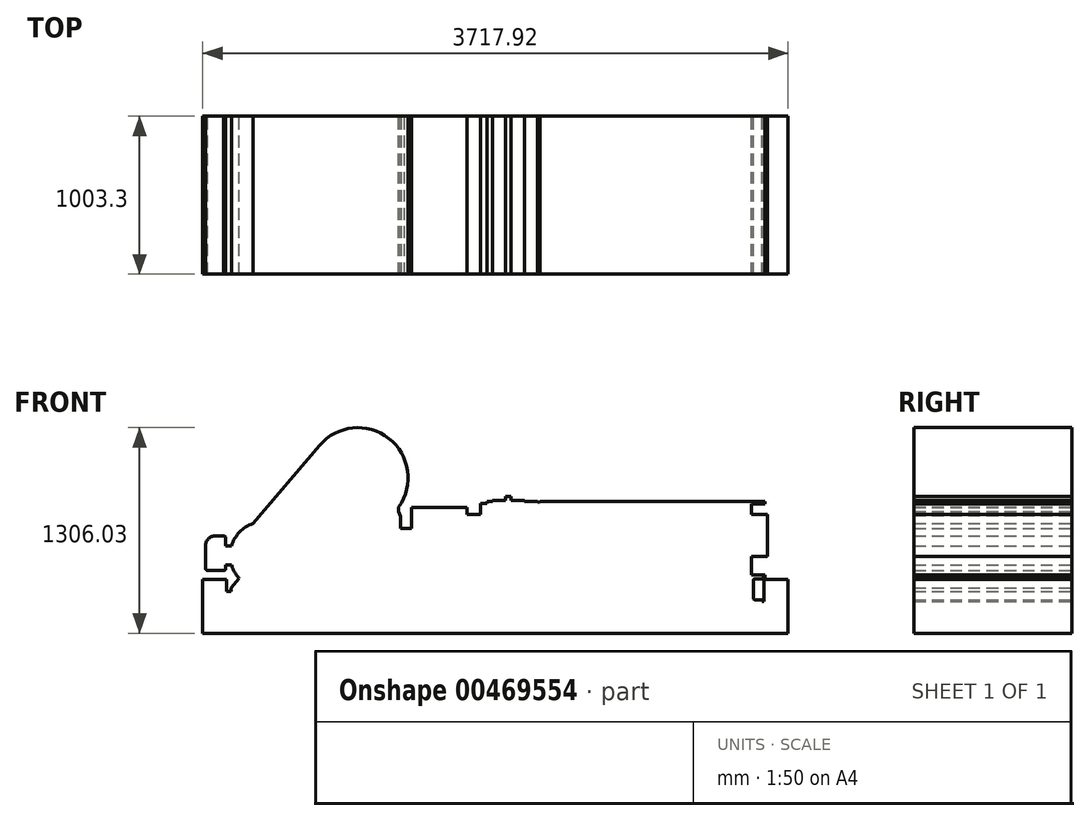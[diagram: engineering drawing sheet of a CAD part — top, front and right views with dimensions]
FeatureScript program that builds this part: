
annotation { "Feature Type Name" : "Feature", "Feature Type Description" : "" }
export const myFeature = defineFeature(function(context is Context, id is Id, definition is map)
    precondition{}
    {
        {
            var Q0;
            Q0=qCreatedBy(makeId("Front.planeOp"),FACE);
            var sketch = newSketch(context, id + "F0", { "sketchPlane" : qUnion([Q0])});
            skLineSegment(sketch, "E0", {"start": v(-2232.26, -692.1) * mm, "end": v(-2341.03, -692.1) * mm});
            skLineSegment(sketch, "E1", {"start": v(-2232.2, -756.28) * mm, "end": v(-2232.2, -692.78) * mm});
            skLineSegment(sketch, "E2", {"start": v(-2939.48, -959.48) * mm, "end": v(-2939.48, -616.58) * mm});
            skLineSegment(sketch, "E3", {"start": v(-2232.2, -756.28) * mm, "end": v(-2223.12, -756.28) * mm});
            skLineSegment(sketch, "E4", {"start": v(613.26, -603.88) * mm, "end": v(632.4, -603.88) * mm});
            skLineSegment(sketch, "E5", {"start": v(613.26, -603.88) * mm, "end": v(613.26, -613.4) * mm});
            skLineSegment(sketch, "E6", {"start": v(613.26, -613.4) * mm, "end": v(568.83, -613.4) * mm});
            skArc(sketch, "E7", {"start": v(568.83, -613.4) * mm, "mid": v(560.97, -616.66) * mm, "end": v(557.72, -624.52) * mm});
            skLineSegment(sketch, "E8", {"start": v(557.72, -624.52) * mm, "end": v(557.72, -735.64) * mm});
            skArc(sketch, "E9", {"start": v(557.72, -735.64) * mm, "mid": v(560.97, -743.5) * mm, "end": v(568.83, -746.76) * mm});
            skLineSegment(sketch, "E10", {"start": v(568.83, -746.76) * mm, "end": v(613.26, -746.76) * mm});
            skLineSegment(sketch, "E11", {"start": v(613.26, -746.76) * mm, "end": v(613.26, -756.28) * mm});
            skLineSegment(sketch, "E12", {"start": v(626.04, -756.28) * mm, "end": v(613.26, -756.28) * mm});
            skLineSegment(sketch, "E13", {"start": v(626.04, -616.58) * mm, "end": v(778.44, -616.58) * mm});
            skLineSegment(sketch, "E14", {"start": v(626.04, -756.28) * mm, "end": v(626.04, -616.58) * mm});
            skLineSegment(sketch, "E15", {"start": v(-2939.48, -616.58) * mm, "end": v(-2787.08, -616.58) * mm});
            skLineSegment(sketch, "E16", {"start": v(-2787.15, -615.9) * mm, "end": v(-2787.15, -692.1) * mm});
            skLineSegment(sketch, "E17", {"start": v(-1646.16, -294.38) * mm, "end": v(-1613.7, -294.38) * mm});
            skArc(sketch, "E18", {"start": v(-1657.28, -292.97) * mm, "mid": v(-1651.76, -294.02) * mm, "end": v(-1646.16, -294.38) * mm});
            skLineSegment(sketch, "E19", {"start": v(-1682.8, -210.41) * mm, "end": v(-1682.8, -292.17) * mm});
            skLineSegment(sketch, "E20", {"start": v(-1657.14, -292.97) * mm, "end": v(-1675.74, -292.97) * mm});
            skLineSegment(sketch, "E21", {"start": v(-1675.74, -292.97) * mm, "end": v(-1677.12, -292.17) * mm});
            skLineSegment(sketch, "E22", {"start": v(-1677.12, -292.17) * mm, "end": v(-1682.8, -292.17) * mm});
            skLineSegment(sketch, "E23", {"start": v(-1682.8, -210.41) * mm, "end": v(-1685.16, -210.41) * mm});
            skLineSegment(sketch, "E24", {"start": v(-1685.16, -210.41) * mm, "end": v(-1688.25, -201.95) * mm});
            skLineSegment(sketch, "E25", {"start": v(-1688.25, -201.95) * mm, "end": v(-1694.41, -185.01) * mm});
            skArc(sketch, "E26", {"start": v(-2793.57, -353.14) * mm, "mid": v(-2797.71, -343.76) * mm, "end": v(-2807.44, -340.5) * mm});
            skLineSegment(sketch, "E27", {"start": v(-2793.57, -404.73) * mm, "end": v(-2793.57, -353.14) * mm});
            skArc(sketch, "E28", {"start": v(-2802.3, -559.51) * mm, "mid": v(-2796.13, -556.96) * mm, "end": v(-2793.57, -550.78) * mm});
            skLineSegment(sketch, "E29", {"start": v(-2793.57, -550.78) * mm, "end": v(-2793.57, -524.48) * mm});
            skLineSegment(sketch, "E30", {"start": v(-2802.3, -559.51) * mm, "end": v(-2907.87, -559.51) * mm});
            skArc(sketch, "E31", {"start": v(-2755.97, -525.47) * mm, "mid": v(-2736.79, -570.37) * mm, "end": v(-2707.94, -609.76) * mm});
            skArc(sketch, "E32", {"start": v(-2619.82, -262.14) * mm, "mid": v(-2705.04, -316.44) * mm, "end": v(-2755.9, -403.74) * mm});
            skArc(sketch, "E33", {"start": v(-2340.97, -673.8) * mm, "mid": v(-2341.16, -672.7) * mm, "end": v(-2341.71, -671.75) * mm});
            skLineSegment(sketch, "E34", {"start": v(-2341.71, -671.75) * mm, "end": v(-2406.21, -594.89) * mm});
            skLineSegment(sketch, "E35", {"start": v(-2341.03, -673.12) * mm, "end": v(-2341.03, -692.1) * mm});
            skLineSegment(sketch, "E36", {"start": v(-2760.13, -671.96) * mm, "end": v(-2760.13, -692.1) * mm});
            skLineSegment(sketch, "E37", {"start": v(-2760.13, -671.96) * mm, "end": v(-2707.94, -609.76) * mm});
            skLineSegment(sketch, "E38", {"start": v(-2793.57, -404.73) * mm, "end": v(-2755.9, -403.74) * mm});
            skLineSegment(sketch, "E39", {"start": v(-2793.57, -524.48) * mm, "end": v(-2755.97, -525.47) * mm});
            skLineSegment(sketch, "E40", {"start": v(-2858.24, -340.5) * mm, "end": v(-2807.44, -340.5) * mm});
            skArc(sketch, "E41", {"start": v(-2921.74, -546.87) * mm, "mid": v(-2917.6, -556.25) * mm, "end": v(-2907.87, -559.51) * mm});
            skLineSegment(sketch, "E42", {"start": v(-2921.74, -546.87) * mm, "end": v(-2921.74, -404) * mm});
            skArc(sketch, "E43", {"start": v(-2858.24, -340.5) * mm, "mid": v(-2903.14, -359.1) * mm, "end": v(-2921.74, -404) * mm});
            skLineSegment(sketch, "E44", {"start": v(-2619.82, -262.14) * mm, "end": v(-2197.96, 234.08) * mm});
            skLineSegment(sketch, "E45", {"start": v(-2406.21, -594.89) * mm, "end": v(-2223.12, -491.34) * mm});
            skLineSegment(sketch, "E46", {"start": v(646.68, -470.53) * mm, "end": v(646.68, -203.83) * mm});
            skLineSegment(sketch, "E47", {"start": v(-896.37, -114.93) * mm, "end": v(-980.5, -114.93) * mm});
            skLineSegment(sketch, "E48", {"start": v(-1099.57, -114.93) * mm, "end": v(-1099.57, -121.28) * mm});
            skLineSegment(sketch, "E49", {"start": v(-896.37, -121.28) * mm, "end": v(-896.37, -114.93) * mm});
            skLineSegment(sketch, "E50", {"start": v(-1015.43, -89.53) * mm, "end": v(-1015.43, -114.93) * mm});
            skLineSegment(sketch, "E51", {"start": v(-980.5, -114.93) * mm, "end": v(-980.5, -89.53) * mm});
            skLineSegment(sketch, "E52", {"start": v(-980.5, -89.53) * mm, "end": v(-1015.43, -89.53) * mm});
            skLineSegment(sketch, "E53", {"start": v(-1148.78, -133.98) * mm, "end": v(-1174.18, -133.98) * mm});
            skLineSegment(sketch, "E54", {"start": v(-1174.18, -133.98) * mm, "end": v(-1174.18, -203.83) * mm});
            skLineSegment(sketch, "E55", {"start": v(-1174.18, -203.83) * mm, "end": v(-1259.06, -203.83) * mm});
            skLineSegment(sketch, "E56", {"start": v(-805.88, -129.22) * mm, "end": v(-802.7, -129.22) * mm});
            skLineSegment(sketch, "E57", {"start": v(-812.23, -121.28) * mm, "end": v(-896.37, -121.28) * mm});
            skLineSegment(sketch, "E58", {"start": v(-1132.9, -121.28) * mm, "end": v(-1132.9, -133.98) * mm});
            skLineSegment(sketch, "E59", {"start": v(-812.23, -122.87) * mm, "end": v(-805.88, -129.22) * mm});
            skLineSegment(sketch, "E60", {"start": v(-796.36, -122.87) * mm, "end": v(-796.36, -121.28) * mm});
            skLineSegment(sketch, "E61", {"start": v(-796.36, -122.87) * mm, "end": v(-802.7, -129.22) * mm});
            skLineSegment(sketch, "E62", {"start": v(-1132.9, -133.98) * mm, "end": v(-1148.78, -133.98) * mm});
            skLineSegment(sketch, "E63", {"start": v(632.4, -121.28) * mm, "end": v(-796.36, -121.28) * mm});
            skLineSegment(sketch, "E64", {"start": v(546.67, -588) * mm, "end": v(632.4, -588) * mm});
            skLineSegment(sketch, "E65", {"start": v(632.4, -588) * mm, "end": v(632.4, -603.88) * mm});
            skLineSegment(sketch, "E66", {"start": v(632.4, -137.16) * mm, "end": v(546.67, -137.16) * mm});
            skLineSegment(sketch, "E67", {"start": v(632.4, -121.28) * mm, "end": v(632.4, -137.16) * mm});
            skLineSegment(sketch, "E68", {"start": v(546.67, -203.83) * mm, "end": v(646.68, -203.83) * mm});
            skLineSegment(sketch, "E69", {"start": v(646.68, -470.53) * mm, "end": v(546.67, -470.53) * mm});
            skLineSegment(sketch, "E70", {"start": v(-1259.06, -159.38) * mm, "end": v(-1613.7, -159.38) * mm});
            skLineSegment(sketch, "E71", {"start": v(-1613.7, -159.38) * mm, "end": v(-1613.7, -294.38) * mm});
            skLineSegment(sketch, "E72", {"start": v(-2223.12, -756.28) * mm, "end": v(-2232.2, -756.28) * mm});
            skLineSegment(sketch, "E73", {"start": v(-2223.12, -756.28) * mm, "end": v(-2223.12, -491.34) * mm});
            skLineSegment(sketch, "E74.trimOffspring", {"start": v(-2760.13, -692.1) * mm, "end": v(-2787.15, -692.1) * mm});
            skArc(sketch, "E75.trimOffspring", {"start": v(-1694.88, -158.28) * mm, "mid": v(-1758.36, 279.04) * mm, "end": v(-2197.96, 234.08) * mm});
            skLineSegment(sketch, "E76", {"start": v(-1694.88, -158.28) * mm, "end": v(-1694.41, -185.01) * mm});
            skLineSegment(sketch, "E77.trimOffspring", {"start": v(-1259.06, -203.83) * mm, "end": v(-1259.06, -159.38) * mm});
            skLineSegment(sketch, "E78.trimOffspring", {"start": v(546.67, -470.53) * mm, "end": v(546.67, -588) * mm});
            skLineSegment(sketch, "E79.trimOffspring", {"start": v(546.67, -137.16) * mm, "end": v(546.67, -203.83) * mm});
            skLineSegment(sketch, "E80.trimOffspring", {"start": v(-1099.57, -121.28) * mm, "end": v(-1132.9, -121.28) * mm});
            skLineSegment(sketch, "E81.trimOffspring", {"start": v(-1015.43, -114.93) * mm, "end": v(-1099.57, -114.93) * mm});
            skLineSegment(sketch, "E82.trimOffspring", {"start": v(-812.23, -122.87) * mm, "end": v(-812.23, -121.28) * mm});
            skLineSegment(sketch, "E83", {"start": v(778.44, -616.58) * mm, "end": v(778.44, -959.48) * mm});
            skLineSegment(sketch, "E84", {"start": v(778.44, -959.48) * mm, "end": v(-2939.48, -959.48) * mm});
            skSolve(sketch);
        }
        {
            var Q0;
            {var subQ0=sQuery(id+"F0.wireOp",EDGE,"E2");Q0=makeQuery(id+"F0.imprint","IMPRINT",FACE,{"disambiguationData":[TD([[makeQuery(id+"F0.imprint","IMPRINT",EDGE,{"derivedFrom":subQ0}),-1.0]])]});}
            extrude(context, id + "F1", {"entities" : qUnion([Q0]), "depth" : 1003.3 * mm, "offsetDistance" : 25.4 * mm});
        }
    });
